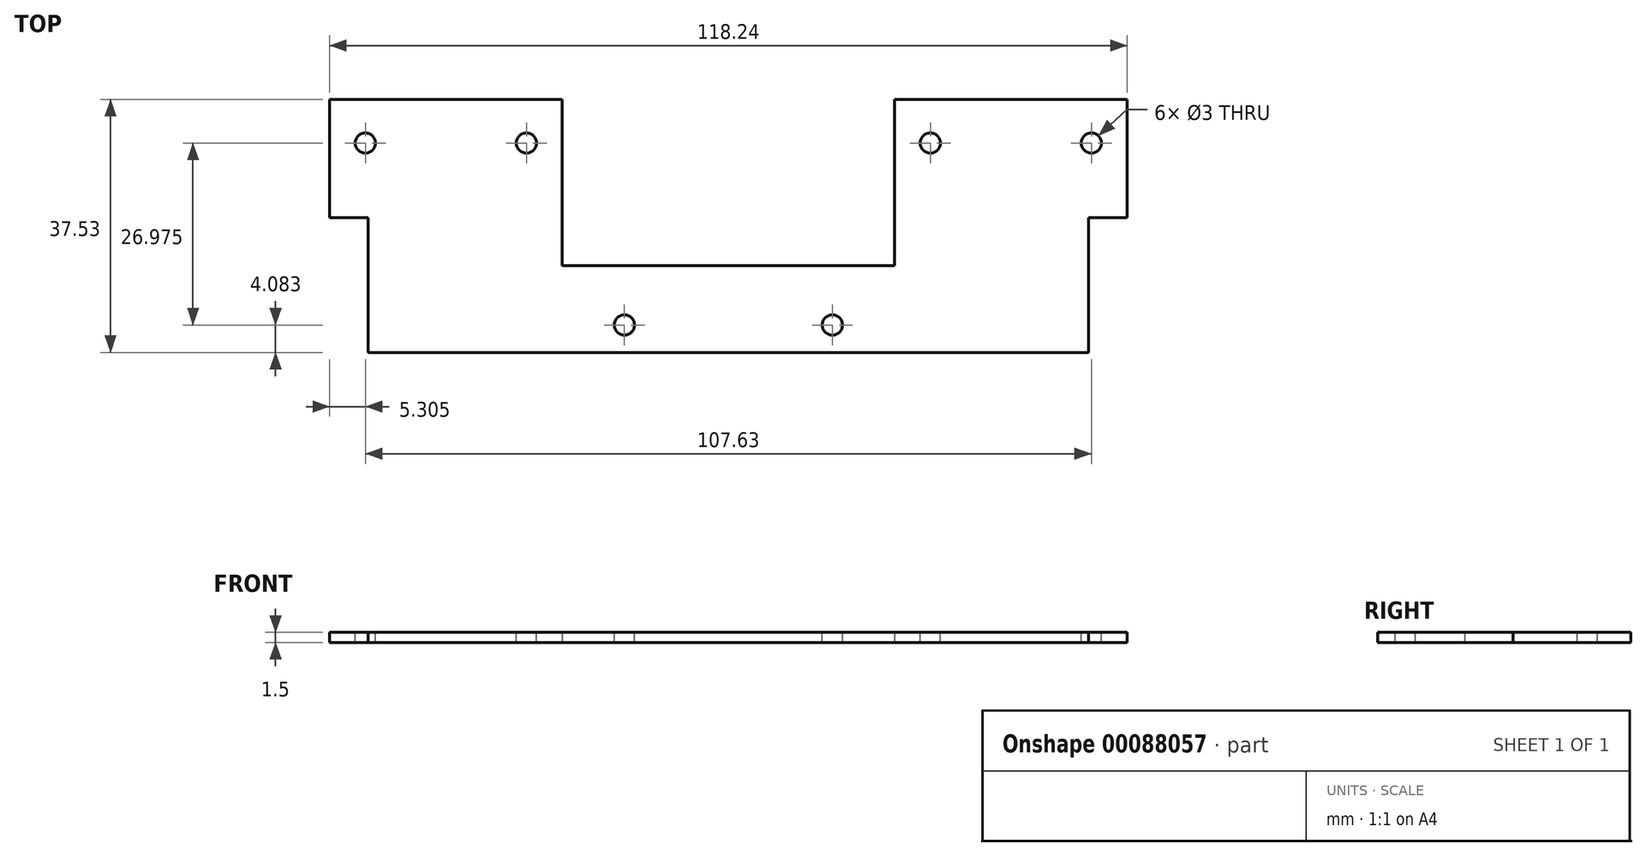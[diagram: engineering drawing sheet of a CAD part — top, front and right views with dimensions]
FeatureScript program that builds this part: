
annotation { "Feature Type Name" : "Feature", "Feature Type Description" : "" }
export const myFeature = defineFeature(function(context is Context, id is Id, definition is map)
    precondition{}
    {
        {
            var Q0;
            Q0=qCreatedBy(makeId("Top.planeOp"),FACE);
            var sketch = newSketch(context, id + "F0", { "sketchPlane" : qUnion([Q0])});
            skLineSegment(sketch, "E0", {"start": v(0, 8.12) * mm, "end": v(-53.42, 8.12) * mm});
            skLineSegment(sketch, "E1", {"start": v(0, 21) * mm, "end": v(-24.64, 21) * mm});
            skLineSegment(sketch, "E2", {"start": v(-24.64, 21) * mm, "end": v(-24.64, 45.65) * mm});
            skLineSegment(sketch, "E3", {"start": v(-24.64, 45.65) * mm, "end": v(-59.12, 45.65) * mm});
            skLineSegment(sketch, "E4", {"start": v(-59.12, 45.65) * mm, "end": v(-59.12, 28.13) * mm});
            skLineSegment(sketch, "E5", {"start": v(-59.12, 28.13) * mm, "end": v(-53.42, 28.13) * mm});
            skLineSegment(sketch, "E6", {"start": v(-53.42, 28.13) * mm, "end": v(-53.42, 8.12) * mm});
            skLineSegment(sketch, "E7", {"start": v(0, -14.62) * mm, "end": v(0, 65.65) * mm, "construction": true});
            skPoint(sketch, "E8.end.orphan", {"position": v(24.46, 45.65) * mm});
            skLineSegment(sketch, "E9.MirrorCS", {"start": v(0, 8.12) * mm, "end": v(53.42, 8.12) * mm});
            skLineSegment(sketch, "E10.MirrorCS", {"start": v(53.42, 28.13) * mm, "end": v(53.42, 8.12) * mm});
            skLineSegment(sketch, "E11.MirrorCS", {"start": v(59.12, 28.13) * mm, "end": v(53.42, 28.13) * mm});
            skLineSegment(sketch, "E12.MirrorCS", {"start": v(59.12, 45.65) * mm, "end": v(59.12, 28.13) * mm});
            skLineSegment(sketch, "E13.MirrorCS", {"start": v(24.64, 45.65) * mm, "end": v(59.12, 45.65) * mm});
            skLineSegment(sketch, "E14.MirrorCS", {"start": v(24.64, 21) * mm, "end": v(24.64, 45.65) * mm});
            skLineSegment(sketch, "E15.MirrorCS", {"start": v(0, 21) * mm, "end": v(24.64, 21) * mm});
            skSolve(sketch);
        }
        {
            var Q0;
            Q0 = qSketchRegion(id + "F0", true);
            extrude(context, id + "F1", {"entities" : qUnion([Q0]), "depth" : 1.5 * mm, "offsetDistance" : 25 * mm});
        }
        {
            var Q0;
            Q0=makeQuery(id+"F1.opExtrude","CAP_FACE",FACE,{"disambiguationData":[OSD([sQuery(id+"F0.wireOp",EDGE,"E0"),sQuery(id+"F0.wireOp",EDGE,"E1"),sQuery(id+"F0.wireOp",EDGE,"E2"),sQuery(id+"F0.wireOp",EDGE,"E3"),sQuery(id+"F0.wireOp",EDGE,"E4"),sQuery(id+"F0.wireOp",EDGE,"E5"),sQuery(id+"F0.wireOp",EDGE,"E6"),sQuery(id+"F0.wireOp",EDGE,"E9.MirrorCS"),sQuery(id+"F0.wireOp",EDGE,"E10.MirrorCS"),sQuery(id+"F0.wireOp",EDGE,"E11.MirrorCS"),sQuery(id+"F0.wireOp",EDGE,"E12.MirrorCS"),sQuery(id+"F0.wireOp",EDGE,"E13.MirrorCS"),sQuery(id+"F0.wireOp",EDGE,"E14.MirrorCS"),sQuery(id+"F0.wireOp",EDGE,"E15.MirrorCS")])],"isStart":false});
            var sketch = newSketch(context, id + "F2", { "sketchPlane" : qUnion([Q0])});
            skCircle(sketch, "E16", {"center": v(-53.82, 39.18) * mm, "radius": 1.5 * mm});
            skCircle(sketch, "E17", {"center": v(-29.94, 39.18) * mm, "radius": 1.5 * mm});
            skCircle(sketch, "E18", {"center": v(-15.42, 12.2) * mm, "radius": 1.5 * mm});
            skLineSegment(sketch, "E19", {"start": v(0, 0) * mm, "end": v(0, 51.81) * mm, "construction": true});
            skCircle(sketch, "E20.MirrorC", {"center": v(15.42, 12.2) * mm, "radius": 1.5 * mm});
            skCircle(sketch, "E21.MirrorC", {"center": v(29.94, 39.18) * mm, "radius": 1.5 * mm});
            skCircle(sketch, "E22.MirrorC", {"center": v(53.82, 39.18) * mm, "radius": 1.5 * mm});
            skSolve(sketch);
        }
        {
            var Q0;
            Q0 = qSketchRegion(id + "F2", true);
            extrude(context, id + "F3", {"entities" : qUnion([Q0]), "operationType" : NewBodyOperationType.REMOVE, "oppositeDirection" : true, "depth" : 12.3 * mm, "offsetDistance" : 25 * mm});
        }
    });
